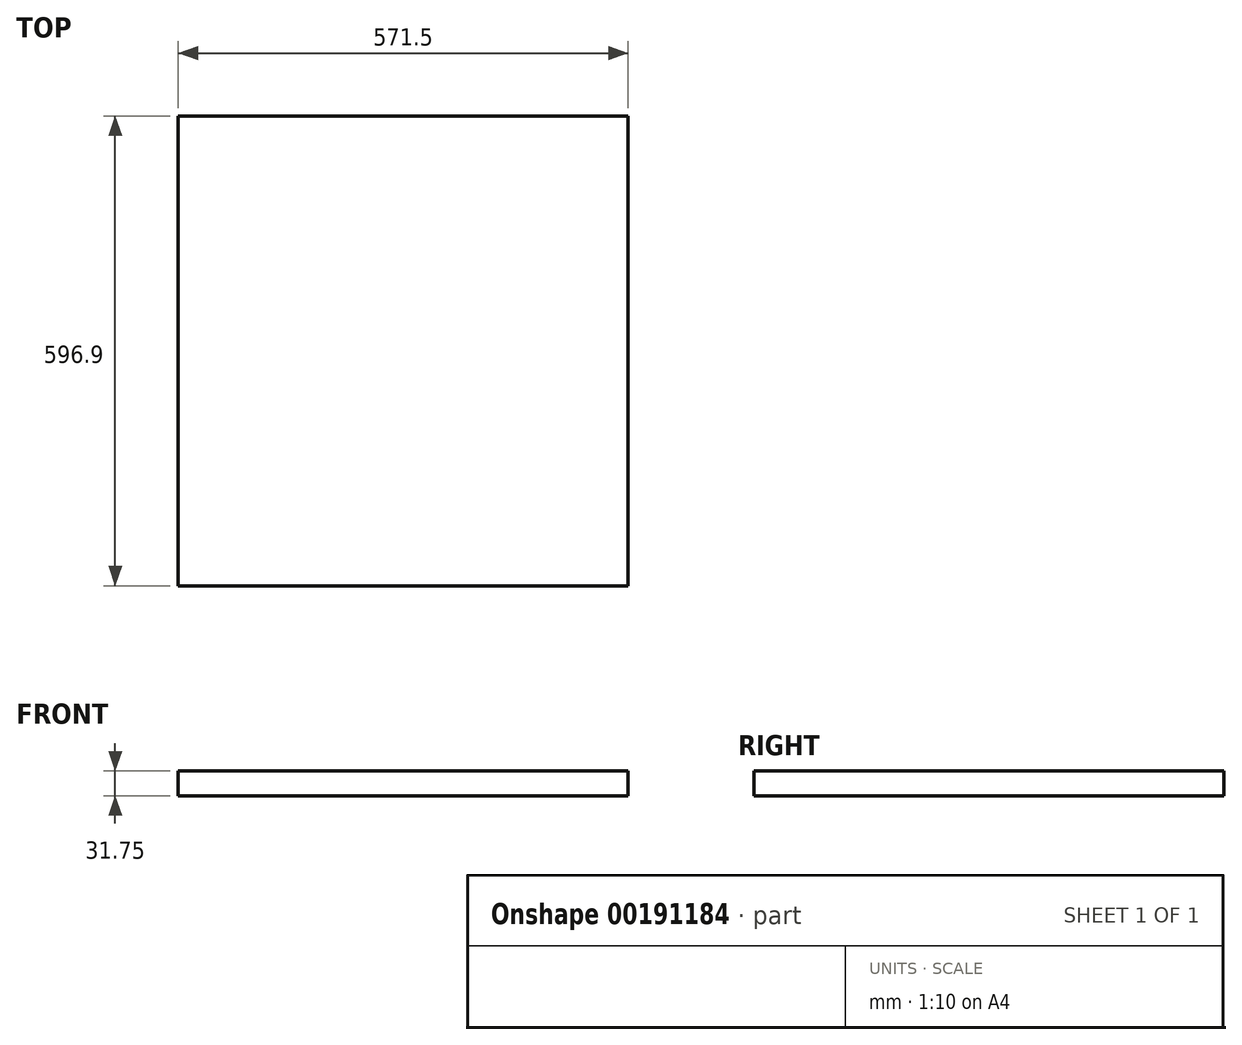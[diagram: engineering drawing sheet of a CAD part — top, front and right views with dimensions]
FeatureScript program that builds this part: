
annotation { "Feature Type Name" : "Feature", "Feature Type Description" : "" }
export const myFeature = defineFeature(function(context is Context, id is Id, definition is map)
    precondition{}
    {
        {
            var Q0;
            Q0=qCreatedBy(makeId("Top.planeOp"),FACE);
            var sketch = newSketch(context, id + "F0", { "sketchPlane" : qUnion([Q0])});
            skLineSegment(sketch, "E0.bottom", {"start": v(285.75, -298.45) * mm, "end": v(-285.75, -298.45) * mm});
            skLineSegment(sketch, "E0.top", {"start": v(285.75, 298.45) * mm, "end": v(-285.75, 298.45) * mm});
            skLineSegment(sketch, "E0.left", {"start": v(285.75, -298.45) * mm, "end": v(285.75, 298.45) * mm});
            skLineSegment(sketch, "E0.right", {"start": v(-285.75, -298.45) * mm, "end": v(-285.75, 298.45) * mm});
            skPoint(sketch, "E0.middle", {"position": v(0, 0) * mm});
            skSolve(sketch);
        }
        {
            var Q0;
            Q0 = qSketchRegion(id + "F0", true);
            extrude(context, id + "F1", {"entities" : qUnion([Q0]), "depth" : 31.75 * mm});
        }
    });
